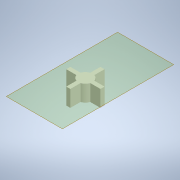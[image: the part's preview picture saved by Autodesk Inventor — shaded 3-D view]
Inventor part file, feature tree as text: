
AUTODESK INVENTOR PART (.ipt)
format: ipt  version: 2022 (Build 260153000, 153)  size: 166,400 bytes
history: native  units: mm
features: extrude x3, sketch x3, other x2, plane x1, projected_geometry x1
ambient origin geometry x8: Origin, YZ Plane, XZ Plane, XY Plane, X Axis, Y Axis, Z Axis, Center Point
bodies: Solid1 (feature_tree)
feature tree (10):
  extrude  "Extrusion1"  Depth=2.0mm
  extrude  "Extrusion2"  Depth=5.0mm TaperAngle=360.0deg
  sketch  "Sketch3"  dims[d7=3.329203mm d8=10.400271mm d9=3.535534mm d10=5.0mm d11=0.0mm d12=5.2mm d13=3.2mm d14=3.0mm d15=0.0mm d16=10.0mm d17=0.0mm]
  plane  "Work Plane1"
  extrude  "Extrusion3"  Depth=10.0mm
  sketch  "Sketch1"  dims[d0=7.0mm d1=2.0mm]
  sketch  "Sketch2"  dims[d2=5.0mm d3=40.0mm d5=360.0deg]
  projected_geometry  "Projected Loop1"
  other  "Assembly2"
  other  "body:1"
